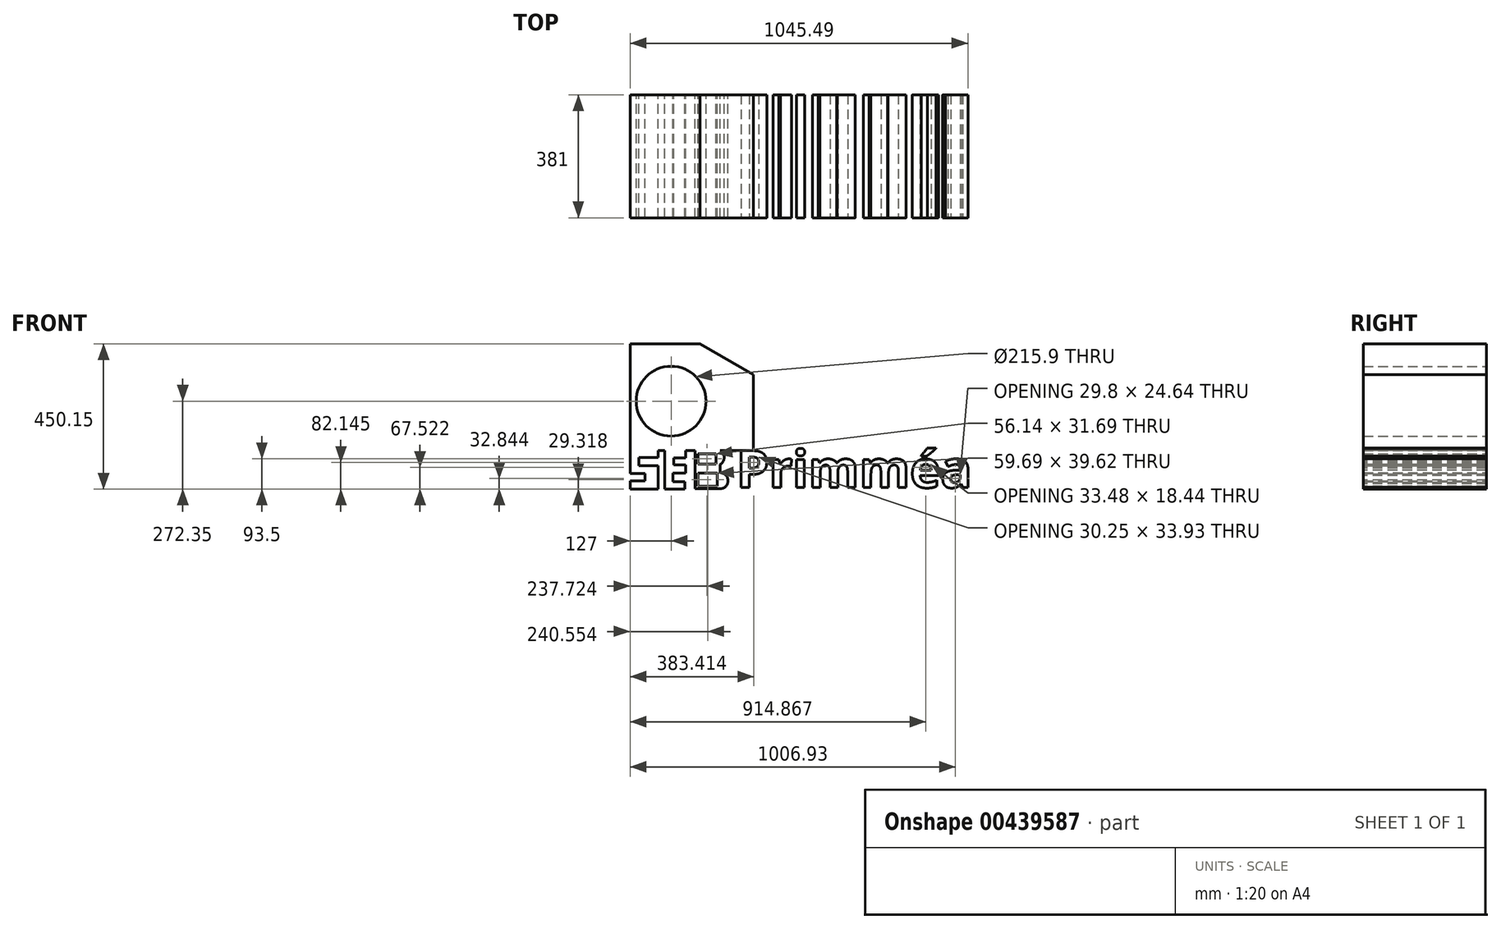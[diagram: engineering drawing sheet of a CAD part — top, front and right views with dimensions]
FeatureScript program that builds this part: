
annotation { "Feature Type Name" : "Feature", "Feature Type Description" : "" }
export const myFeature = defineFeature(function(context is Context, id is Id, definition is map)
    precondition{}
    {
        {
            var Q0;
            Q0=qCreatedBy(makeId("Front.planeOp"),FACE);
            var sketch = newSketch(context, id + "F0", { "sketchPlane" : qUnion([Q0])});
            skLineSegment(sketch, "E0", {"start": v(0, 0) * mm, "end": v(0, 330.2) * mm});
            skLineSegment(sketch, "E1", {"start": v(0, 330.2) * mm, "end": v(215.9, 330.2) * mm});
            skLineSegment(sketch, "E2", {"start": v(381, 234.88) * mm, "end": v(215.9, 330.2) * mm});
            skLineSegment(sketch, "E3", {"start": v(0, 0) * mm, "end": v(381, 0) * mm});
            skLineSegment(sketch, "E4", {"start": v(381, 234.88) * mm, "end": v(381, 0) * mm});
            skCircle(sketch, "E5", {"center": v(127, 152.4) * mm, "radius": 107.95 * mm});
            skSolve(sketch);
        }
        {
            var Q0;
            Q0 = qSketchRegion(id + "F0", true);
            extrude(context, id + "F1", {"entities" : qUnion([Q0]), "endBound" : BoundingType.SYMMETRIC, "depth" : 381 * mm});
        }
        {
            var Q0;
            Q0=qCreatedBy(makeId("Front.planeOp"),FACE);
            var sketch = newSketch(context, id + "F2", { "sketchPlane" : qUnion([Q0])});
            skLineSegment(sketch, "E6", {"start": v(0, 0) * mm, "end": v(86.68, 0) * mm});
            skLineSegment(sketch, "E7", {"start": v(86.68, 0) * mm, "end": v(86.68, -22.34) * mm});
            skLineSegment(sketch, "E8", {"start": v(86.68, -22.34) * mm, "end": v(26.74, -22.34) * mm});
            skLineSegment(sketch, "E9", {"start": v(26.74, -22.34) * mm, "end": v(26.74, -47.54) * mm});
            skLineSegment(sketch, "E10", {"start": v(26.74, -47.54) * mm, "end": v(86.68, -47.54) * mm});
            skLineSegment(sketch, "E11", {"start": v(0, 0) * mm, "end": v(0, -71.3) * mm});
            skLineSegment(sketch, "E12", {"start": v(0, -71.3) * mm, "end": v(45.97, -71.3) * mm});
            skLineSegment(sketch, "E13", {"start": v(45.97, -71.3) * mm, "end": v(45.97, -95.04) * mm});
            skLineSegment(sketch, "E14", {"start": v(45.97, -95.04) * mm, "end": v(0, -95.04) * mm});
            skLineSegment(sketch, "E15", {"start": v(0, -95.04) * mm, "end": v(0, -119.93) * mm});
            skLineSegment(sketch, "E16", {"start": v(0, -119.93) * mm, "end": v(86.68, -119.93) * mm});
            skLineSegment(sketch, "E17", {"start": v(86.68, -119.93) * mm, "end": v(86.68, -47.54) * mm});
            skLineSegment(sketch, "E18", {"start": v(107.17, 0) * mm, "end": v(107.17, -119.95) * mm});
            skLineSegment(sketch, "E19", {"start": v(107.17, -119.95) * mm, "end": v(170.03, -119.95) * mm});
            skLineSegment(sketch, "E20", {"start": v(170.03, -119.95) * mm, "end": v(170.03, -97.24) * mm});
            skLineSegment(sketch, "E21", {"start": v(170.03, -97.24) * mm, "end": v(132.53, -97.24) * mm});
            skLineSegment(sketch, "E22", {"start": v(132.53, -97.24) * mm, "end": v(132.53, -69.77) * mm});
            skLineSegment(sketch, "E23", {"start": v(132.53, -69.77) * mm, "end": v(171.62, -69.77) * mm});
            skLineSegment(sketch, "E24", {"start": v(171.62, -69.77) * mm, "end": v(171.62, -45.47) * mm});
            skLineSegment(sketch, "E25", {"start": v(171.62, -45.47) * mm, "end": v(135.7, -45.47) * mm});
            skLineSegment(sketch, "E26", {"start": v(135.7, -45.47) * mm, "end": v(135.7, -23.8) * mm});
            skLineSegment(sketch, "E27", {"start": v(135.7, -23.8) * mm, "end": v(171.62, -23.8) * mm});
            skLineSegment(sketch, "E28", {"start": v(171.62, -23.8) * mm, "end": v(171.62, 0) * mm});
            skLineSegment(sketch, "E29", {"start": v(171.62, 0) * mm, "end": v(107.17, 0) * mm});
            skLineSegment(sketch, "E30", {"start": v(200.67, 0) * mm, "end": v(200.67, -118.9) * mm});
            skLineSegment(sketch, "E31", {"start": v(200.67, -118.9) * mm, "end": v(278.32, -118.9) * mm});
            skLineSegment(sketch, "E32", {"start": v(200.67, 0) * mm, "end": v(278.32, 0) * mm});
            skLineSegment(sketch, "E33", {"start": v(278.32, -43.83) * mm, "end": v(278.32, -69.24) * mm});
            skArc(sketch, "E34", {"start": v(278.32, -43.83) * mm, "mid": v(291.04, -21.91) * mm, "end": v(278.32, 0) * mm});
            skArc(sketch, "E35", {"start": v(278.32, -118.9) * mm, "mid": v(303.15, -94.06) * mm, "end": v(278.32, -69.24) * mm});
            skLineSegment(sketch, "E36.bottom", {"start": v(209.65, -10.6) * mm, "end": v(265.8, -10.6) * mm});
            skLineSegment(sketch, "E36.top", {"start": v(209.65, -42.3) * mm, "end": v(265.8, -42.3) * mm});
            skLineSegment(sketch, "E36.left", {"start": v(209.65, -10.6) * mm, "end": v(209.65, -42.3) * mm});
            skLineSegment(sketch, "E36.right", {"start": v(265.8, -10.6) * mm, "end": v(265.8, -42.3) * mm});
            skLineSegment(sketch, "E37.bottom", {"start": v(210.7, -70.82) * mm, "end": v(270.4, -70.82) * mm});
            skLineSegment(sketch, "E37.top", {"start": v(210.7, -110.44) * mm, "end": v(270.4, -110.44) * mm});
            skLineSegment(sketch, "E37.left", {"start": v(210.7, -70.82) * mm, "end": v(210.7, -110.44) * mm});
            skLineSegment(sketch, "E37.right", {"start": v(270.4, -70.82) * mm, "end": v(270.4, -110.44) * mm});
            skSolve(sketch);
        }
        {
            var Q0;
            Q0=makeQuery(id+"F2.imprint","IMPRINT",FACE,{"disambiguationData":[TD([[makeQuery(id+"F2.imprint","IMPRINT",EDGE,{"derivedFrom":sQuery(id+"F2.wireOp",EDGE,"E6")}),-1.0]])]});
            var Q1;
            Q1=makeQuery(id+"F1.opExtrude","CAP_FACE",FACE,{"disambiguationData":[OSD([sQuery(id+"F0.wireOp",EDGE,"E0"),sQuery(id+"F0.wireOp",EDGE,"E1"),sQuery(id+"F0.wireOp",EDGE,"E2"),sQuery(id+"F0.wireOp",EDGE,"E3"),sQuery(id+"F0.wireOp",EDGE,"E4"),sQuery(id+"F0.wireOp",EDGE,"E5")])],"isStart":false});
            var Q2;
            Q2=makeQuery(id+"F1.opExtrude","CAP_FACE",FACE,{"disambiguationData":[OSD([sQuery(id+"F0.wireOp",EDGE,"E0"),sQuery(id+"F0.wireOp",EDGE,"E1"),sQuery(id+"F0.wireOp",EDGE,"E2"),sQuery(id+"F0.wireOp",EDGE,"E3"),sQuery(id+"F0.wireOp",EDGE,"E4"),sQuery(id+"F0.wireOp",EDGE,"E5")])],"isStart":true});
            extrude(context, id + "F3", {"entities" : qUnion([Q0]), "operationType" : NewBodyOperationType.ADD, "endBound" : BoundingType.UP_TO_SURFACE, "endBoundEntityFace" : qUnion([Q1]), "depth" : 500 * mm, "hasSecondDirection" : true, "secondDirectionBound" : SecondDirectionBoundingType.UP_TO_SURFACE, "secondDirectionOppositeDirection" : true, "secondDirectionBoundEntityFace" : qUnion([Q2]), "secondDirectionDepth" : 25 * mm});
        }
        {
            var Q0;
            Q0 = qSketchRegion(id + "F2", true);
            var Q1;
            {var subQ0=sQuery(id+"F0.wireOp",EDGE,"E5");var subQ1=sQuery(id+"F0.wireOp",EDGE,"E4");var subQ2=sQuery(id+"F0.wireOp",EDGE,"E3");var subQ3=sQuery(id+"F0.wireOp",EDGE,"E2");var subQ4=sQuery(id+"F0.wireOp",EDGE,"E1");var subQ5=sQuery(id+"F0.wireOp",EDGE,"E0");Q1=makeQuery(id+"F3.boolean.opBoolean","MERGE",FACE,{"derivedFrom":[makeQuery(id+"F1.opExtrude","CAP_FACE",FACE,{"disambiguationData":[OSD([subQ5,subQ4,subQ3,subQ2,subQ1,subQ0])],"isStart":false}),makeQuery(id+"F3.opExtrude","CAP_FACE",FACE,{"disambiguationData":[OSD([subQ5,subQ4,subQ3,subQ2,subQ1,subQ0])],"isStart":false})]});}
            extrude(context, id + "F4", {"entities" : qUnion([Q0]), "operationType" : NewBodyOperationType.ADD, "endBound" : BoundingType.SYMMETRIC, "endBoundEntityFace" : qUnion([Q1]), "depth" : 381 * mm});
        }
        {
            var Q0;
            {var subQ0=sQuery(id+"F0.wireOp",EDGE,"E5");var subQ1=sQuery(id+"F0.wireOp",EDGE,"E4");var subQ2=sQuery(id+"F0.wireOp",EDGE,"E3");var subQ3=sQuery(id+"F0.wireOp",EDGE,"E2");var subQ4=sQuery(id+"F0.wireOp",EDGE,"E1");var subQ5=sQuery(id+"F0.wireOp",EDGE,"E0");Q0=makeQuery(id+"F4.boolean.opBoolean","MERGE",FACE,{"derivedFrom":[makeQuery(id+"F3.boolean.opBoolean","MERGE",FACE,{"derivedFrom":[makeQuery(id+"F1.opExtrude","CAP_FACE",FACE,{"disambiguationData":[OSD([subQ5,subQ4,subQ3,subQ2,subQ1,subQ0])],"isStart":false}),makeQuery(id+"F3.opExtrude","CAP_FACE",FACE,{"disambiguationData":[OSD([subQ5,subQ4,subQ3,subQ2,subQ1,subQ0])],"isStart":false})]}),makeQuery(id+"F4.opExtrude","CAP_FACE",FACE,{"disambiguationData":[OSD([sQuery(id+"F2.wireOp",EDGE,"E18"),sQuery(id+"F2.wireOp",EDGE,"E19"),sQuery(id+"F2.wireOp",EDGE,"E20"),sQuery(id+"F2.wireOp",EDGE,"E21"),sQuery(id+"F2.wireOp",EDGE,"E22"),sQuery(id+"F2.wireOp",EDGE,"E23"),sQuery(id+"F2.wireOp",EDGE,"E24"),sQuery(id+"F2.wireOp",EDGE,"E25"),sQuery(id+"F2.wireOp",EDGE,"E26"),sQuery(id+"F2.wireOp",EDGE,"E27"),sQuery(id+"F2.wireOp",EDGE,"E28"),sQuery(id+"F2.wireOp",EDGE,"E29")])],"isStart":false}),makeQuery(id+"F4.opExtrude","CAP_FACE",FACE,{"disambiguationData":[OSD([sQuery(id+"F2.wireOp",EDGE,"E30"),sQuery(id+"F2.wireOp",EDGE,"E31"),sQuery(id+"F2.wireOp",EDGE,"E32"),sQuery(id+"F2.wireOp",EDGE,"E33"),sQuery(id+"F2.wireOp",EDGE,"E34"),sQuery(id+"F2.wireOp",EDGE,"E35"),sQuery(id+"F2.wireOp",EDGE,"E36.bottom"),sQuery(id+"F2.wireOp",EDGE,"E36.top"),sQuery(id+"F2.wireOp",EDGE,"E36.left"),sQuery(id+"F2.wireOp",EDGE,"E36.right"),sQuery(id+"F2.wireOp",EDGE,"E37.bottom"),sQuery(id+"F2.wireOp",EDGE,"E37.top"),sQuery(id+"F2.wireOp",EDGE,"E37.left"),sQuery(id+"F2.wireOp",EDGE,"E37.right")])],"isStart":false})]});}
            var sketch = newSketch(context, id + "F5", { "sketchPlane" : qUnion([Q0])});
            skText(sketch, "E38", { "text": "Primméa", "fontName": "OpenSans-Bold.ttf"});
            const initialGuessF5  = {"E38": [0.32966, -0.11529, 1, 0, 0.11529]};
            skSetInitialGuess(sketch, initialGuessF5);
            skSolve(sketch);
        }
        {
            var Q0;
            Q0 = qSketchRegion(id + "F5", true);
            extrude(context, id + "F6", {"entities" : qUnion([Q0]), "oppositeDirection" : true, "depth" : 381 * mm});
        }
    });
